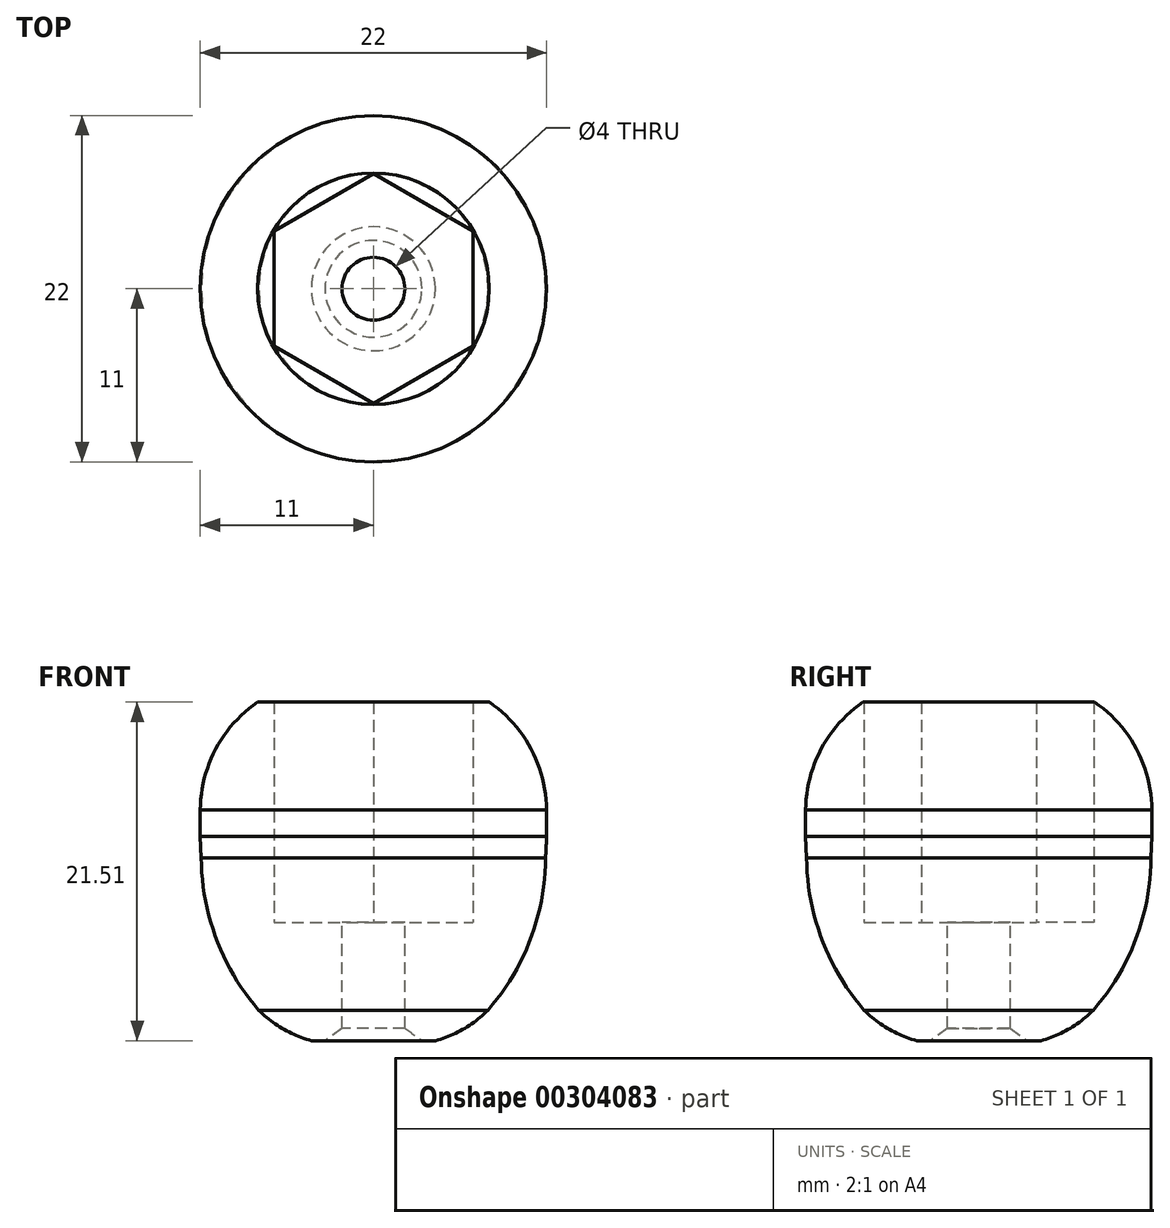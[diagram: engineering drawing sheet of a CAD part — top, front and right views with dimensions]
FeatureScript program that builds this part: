
annotation { "Feature Type Name" : "Feature", "Feature Type Description" : "" }
export const myFeature = defineFeature(function(context is Context, id is Id, definition is map)
    precondition{}
    {
        {
            var Q0;
            Q0=qCreatedBy(makeId("Front.planeOp"),FACE);
            var sketch = newSketch(context, id + "F0", { "sketchPlane" : qUnion([Q0])});
            skPoint(sketch, "E0.endSnap0", {"position": v(3.5, 4.5) * mm});
            skLineSegment(sketch, "E1", {"start": v(2, 0.79) * mm, "end": v(3.07, 0) * mm});
            skPoint(sketch, "E2.startSnap0", {"position": v(11, 11) * mm});
            skArc(sketch, "E3", {"start": v(2, 11.53) * mm, "mid": v(4.8, 13.4) * mm, "end": v(5.74, 16.64) * mm});
            skLineSegment(sketch, "E4", {"start": v(2, 11.53) * mm, "end": v(2, 0.79) * mm});
            skLineSegment(sketch, "E5", {"start": v(5.74, 16.64) * mm, "end": v(5.74, 20.68) * mm});
            skArc(sketch, "E6", {"start": v(11, 14.67) * mm, "mid": v(10.1, 18.37) * mm, "end": v(7.64, 21.3) * mm});
            skPoint(sketch, "E7.visualSharp", {"position": v(6.53, 22) * mm});
            skLineSegment(sketch, "E8", {"start": v(11, 14.67) * mm, "end": v(11, 12.97) * mm});
            skLineSegment(sketch, "E9", {"start": v(3.94, 0) * mm, "end": v(3.07, 0) * mm});
            skLineSegment(sketch, "E10", {"start": v(0, 12.28) * mm, "end": v(0, 4.07) * mm});
            skArc(sketch, "E11", {"start": v(7.28, 1.94) * mm, "mid": v(9.97, 6.45) * mm, "end": v(10.94, 11.61) * mm});
            skPoint(sketch, "E12.visualSharp", {"position": v(11, 12.78) * mm});
            skPoint(sketch, "E13.visualSharp", {"position": v(5.25, 0) * mm});
            skArc(sketch, "E14", {"start": v(3.94, 0) * mm, "mid": v(5.74, 0.75) * mm, "end": v(7.28, 1.94) * mm});
            skPoint(sketch, "E15.orphan", {"position": v(4.8, 0) * mm});
            skLineSegment(sketch, "E16", {"start": v(5.74, 20.68) * mm, "end": v(5.74, 21.51) * mm});
            skPoint(sketch, "E16.endSnap0", {"position": v(6.7, 21.51) * mm});
            skLineSegment(sketch, "E17", {"start": v(5.74, 21.51) * mm, "end": v(7.15, 21.51) * mm});
            skLineSegment(sketch, "E18", {"start": v(7.15, 21.51) * mm, "end": v(7.35, 21.51) * mm});
            skLineSegment(sketch, "E19", {"start": v(7.64, 21.3) * mm, "end": v(7.35, 21.51) * mm});
            skLineSegment(sketch, "E20", {"start": v(11, 12.97) * mm, "end": v(10.94, 11.61) * mm});
            skSolve(sketch);
        }
        {
            var Q0;
            Q0=makeQuery(id+"F0.imprint","IMPRINT",FACE,{"disambiguationData":[TD([[makeQuery(id+"F0.imprint","IMPRINT",EDGE,{"derivedFrom":sQuery(id+"F0.wireOp",EDGE,"E1")}),1.0]])]});
            var Q1;
            Q1=sQuery(id+"F0.wireOp",EDGE,"E10");
            revolve(context, id + "F1", {"entities" : qUnion([Q0]), "axis" : qUnion([Q1]), "revolveType" : RevolveType.FULL});
        }
        {
            var Q0;
            Q0=qCreatedBy(makeId("Top.planeOp"),FACE);
            var sketch = newSketch(context, id + "F2", { "sketchPlane" : qUnion([Q0])});
            skCircle(sketch, "E21.cCircle", {"center": v(0, 0) * mm, "radius": 7.3 * mm, "construction": true});
            skLineSegment(sketch, "E21.0", {"start": v(0, 7.3) * mm, "end": v(6.32, 3.65) * mm});
            skLineSegment(sketch, "E21.1", {"start": v(6.32, 3.65) * mm, "end": v(6.32, -3.65) * mm});
            skLineSegment(sketch, "E21.2", {"start": v(6.32, -3.65) * mm, "end": v(0, -7.3) * mm});
            skLineSegment(sketch, "E21.3", {"start": v(0, -7.3) * mm, "end": v(-6.32, -3.65) * mm});
            skLineSegment(sketch, "E21.4", {"start": v(-6.32, -3.65) * mm, "end": v(-6.32, 3.65) * mm});
            skLineSegment(sketch, "E21.5", {"start": v(-6.32, 3.65) * mm, "end": v(0, 7.3) * mm});
            skSolve(sketch);
        }
        {
            var Q0;
            Q0 = qSketchRegion(id + "F2", true);
            extrude(context, id + "F3", {"entities" : qUnion([Q0]), "operationType" : NewBodyOperationType.REMOVE, "depth" : 29.5 * mm, "offsetDistance" : 25 * mm, "hasSecondDirection" : true, "secondDirectionOppositeDirection" : false, "secondDirectionDepth" : 7.5 * mm});
        }
    });
